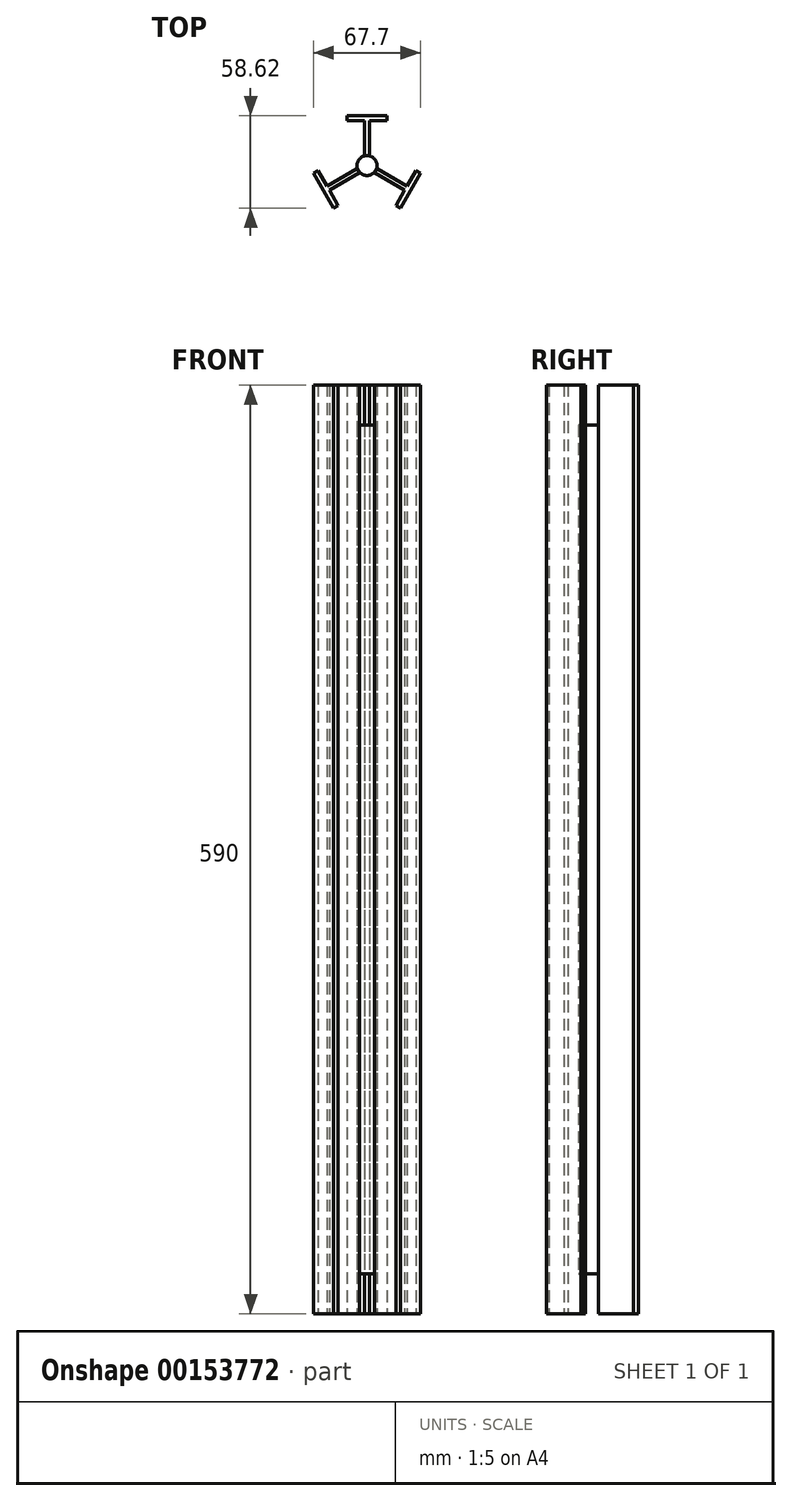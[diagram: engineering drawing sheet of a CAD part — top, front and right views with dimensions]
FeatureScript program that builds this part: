
annotation { "Feature Type Name" : "Feature", "Feature Type Description" : "" }
export const myFeature = defineFeature(function(context is Context, id is Id, definition is map)
    precondition{}
    {
        {
            var Q0;
            Q0=qCreatedBy(makeId("Top.planeOp"),FACE);
            var sketch = newSketch(context, id + "F0", { "sketchPlane" : qUnion([Q0])});
            skLineSegment(sketch, "E0.bottom", {"start": v(-12.7, 31.75) * mm, "end": v(0, 31.75) * mm});
            skLineSegment(sketch, "E0.top", {"start": v(-12.7, 28.58) * mm, "end": v(-1.59, 28.58) * mm});
            skLineSegment(sketch, "E0.left", {"start": v(-12.7, 31.75) * mm, "end": v(-12.7, 28.58) * mm});
            skLineSegment(sketch, "E1.left", {"start": v(-1.59, 28.57) * mm, "end": v(-1.59, 6.35) * mm});
            skPoint(sketch, "E2.MirrorCS.end.orphan", {"position": v(-1.59, 63.5) * mm});
            skPoint(sketch, "E2.MirrorCS.start.orphan", {"position": v(-1.59, 34.92) * mm});
            skPoint(sketch, "E3.MirrorCS.start.orphan", {"position": v(-12.7, 34.92) * mm});
            skPoint(sketch, "E4.MirrorCS.start.orphan", {"position": v(-12.7, 31.75) * mm});
            skPoint(sketch, "E5.orphan", {"position": v(-1.59, 0) * mm});
            skPoint(sketch, "E6.orphan", {"position": v(-1.59, -2.75) * mm});
            skPoint(sketch, "E7.orphan", {"position": v(3.24, 0) * mm});
            skPoint(sketch, "E8.orphan", {"position": v(-1, 3.09) * mm});
            skPoint(sketch, "E9.orphan", {"position": v(1, 3.09) * mm});
            skPoint(sketch, "E10.orphan", {"position": v(1.59, -2.75) * mm});
            skCircle(sketch, "E11", {"center": v(0, 0) * mm, "radius": 6.35 * mm, "construction": true});
            skPoint(sketch, "E12.orphan", {"position": v(4.76, 5) * mm});
            skPoint(sketch, "E13.orphan", {"position": v(-1.59, 5) * mm});
            skPoint(sketch, "E14.orphan", {"position": v(0, -6.35) * mm});
            skPoint(sketch, "E15.MirrorCS.start.orphan", {"position": v(25.4, 5) * mm});
            skPoint(sketch, "E16.0.start.orphan", {"position": v(-25.4, 5) * mm});
            skLineSegment(sketch, "E17.MirrorCS", {"start": v(12.7, 31.75) * mm, "end": v(0, 31.75) * mm});
            skLineSegment(sketch, "E18.MirrorCS", {"start": v(12.7, 31.75) * mm, "end": v(12.7, 28.58) * mm});
            skLineSegment(sketch, "E19.MirrorCS", {"start": v(12.7, 28.58) * mm, "end": v(1.59, 28.58) * mm});
            skLineSegment(sketch, "E20.MirrorCS", {"start": v(1.59, 28.57) * mm, "end": v(1.59, 6.35) * mm});
            skLineSegment(sketch, "E21", {"start": v(-1.59, 6.35) * mm, "end": v(1.59, 6.35) * mm});
            skSolve(sketch);
        }
        {
            var Q0;
            Q0 = qSketchRegion(id + "F0", true);
            extrude(context, id + "F1", {"entities" : qUnion([Q0]), "depth" : 590 * mm});
        }
        {
            var Q0;
            Q0=qCreatedBy(makeId("Top.planeOp"),FACE);
            var sketch = newSketch(context, id + "F2", { "sketchPlane" : qUnion([Q0])});
            skCircle(sketch, "E22", {"center": v(0, 0) * mm, "radius": 6.35 * mm});
            skSolve(sketch);
        }
        {
            var Q0;
            Q0=makeQuery(id+"F1.opExtrude","SWEPT_BODY",BODY,{"disambiguationData":[OSD([sQuery(id+"F0.wireOp",EDGE,"E0.bottom"),sQuery(id+"F0.wireOp",EDGE,"E0.top"),sQuery(id+"F0.wireOp",EDGE,"E0.left"),sQuery(id+"F0.wireOp",EDGE,"E1.left"),sQuery(id+"F0.wireOp",EDGE,"E17.MirrorCS"),sQuery(id+"F0.wireOp",EDGE,"E18.MirrorCS"),sQuery(id+"F0.wireOp",EDGE,"E19.MirrorCS"),sQuery(id+"F0.wireOp",EDGE,"E20.MirrorCS"),sQuery(id+"F0.wireOp",EDGE,"E21")])]});
            var Q1;
            Q1=sQuery(id+"F2.wireOp",EDGE,"E22");
            circularPattern(context, id + "F3", {"operationType" : NewBodyOperationType.ADD, "entities" : qUnion([Q0]), "axis" : qUnion([Q1]), "angle" : 120 * degree, "instanceCount" : 3});
        }
        {
            var Q0;
            Q0=qCreatedBy(makeId("Top.planeOp"),FACE);
            cPlane(context, id + "F4", {"entities" : qUnion([Q0]), "cplaneType" : CPlaneType.OFFSET, "offset" : 295 * mm, "width" : 150 * mm, "height" : 150 * mm});
        }
        {
            var Q0;
            Q0=qCreatedBy(id+"F4.planeOp",FACE);
            var sketch = newSketch(context, id + "F5", { "sketchPlane" : qUnion([Q0])});
            skCircle(sketch, "E23", {"center": v(0, 0) * mm, "radius": 6.35 * mm});
            skSolve(sketch);
        }
        {
            var Q0;
            Q0 = qSketchRegion(id + "F5", true);
            extrude(context, id + "F6", {"entities" : qUnion([Q0]), "endBound" : BoundingType.SYMMETRIC, "depth" : 559 * mm - 20 * mm});
        }
    });
